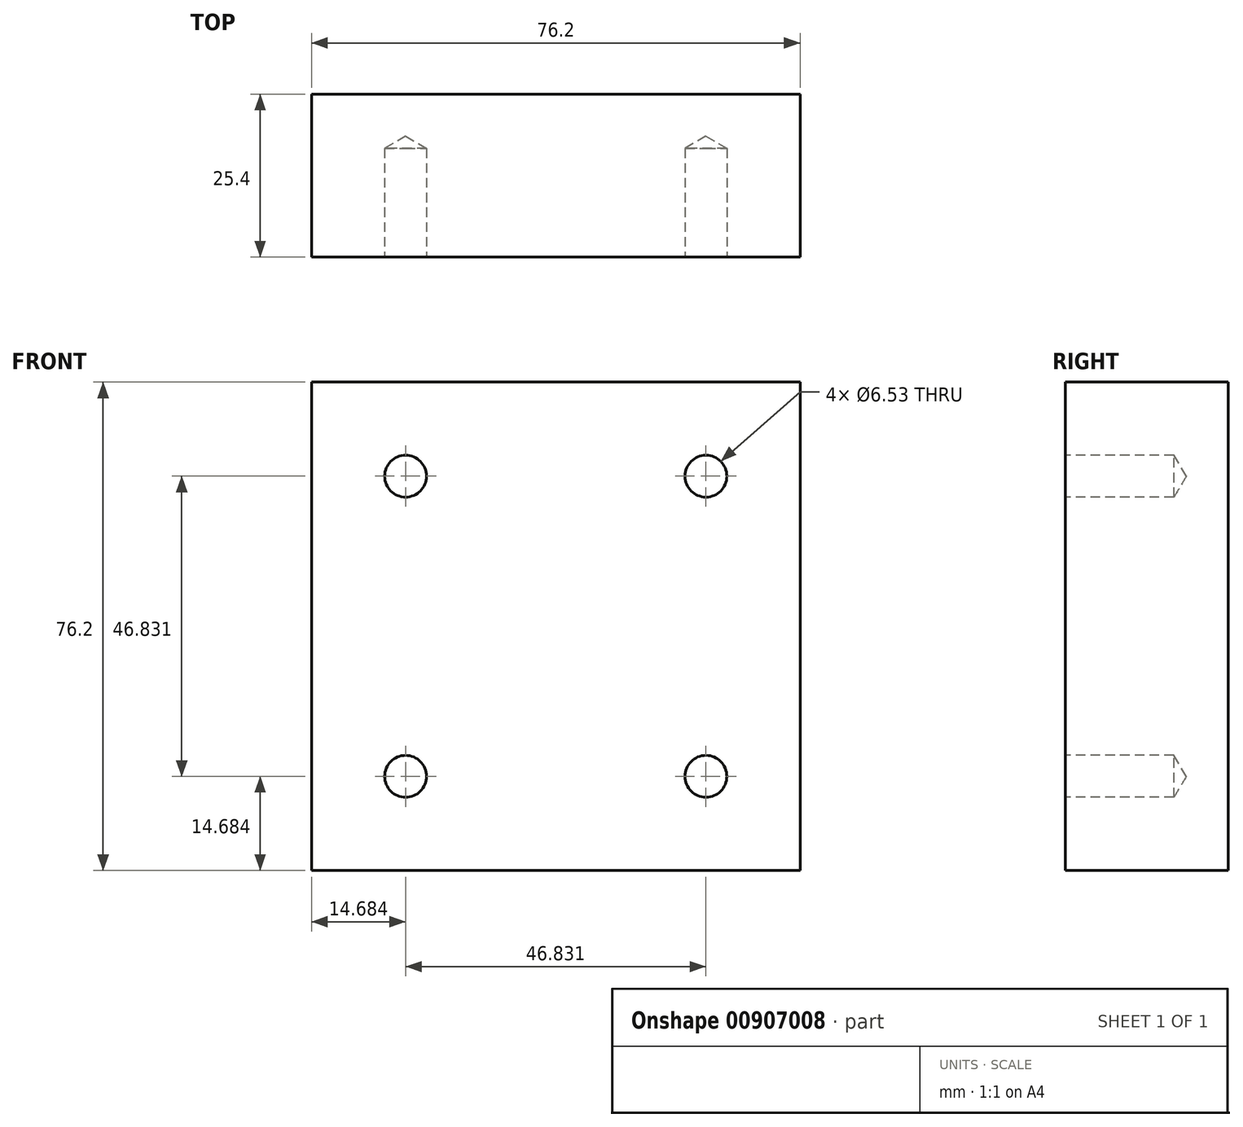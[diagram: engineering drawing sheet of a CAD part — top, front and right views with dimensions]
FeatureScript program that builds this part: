
annotation { "Feature Type Name" : "Feature", "Feature Type Description" : "" }
export const myFeature = defineFeature(function(context is Context, id is Id, definition is map)
    precondition{}
    {
        {
            var Q0;
            Q0=qCreatedBy(makeId("Front.planeOp"),FACE);
            var sketch = newSketch(context, id + "F0", { "sketchPlane" : qUnion([Q0])});
            skLineSegment(sketch, "E0.bottom", {"start": v(38.1, -38.1) * mm, "end": v(-38.1, -38.1) * mm});
            skLineSegment(sketch, "E0.top", {"start": v(38.1, 38.1) * mm, "end": v(-38.1, 38.1) * mm});
            skLineSegment(sketch, "E0.left", {"start": v(38.1, -38.1) * mm, "end": v(38.1, 38.1) * mm});
            skLineSegment(sketch, "E0.right", {"start": v(-38.1, -38.1) * mm, "end": v(-38.1, 38.1) * mm});
            skPoint(sketch, "E0.middle", {"position": v(0, 0) * mm});
            skSolve(sketch);
        }
        {
            var Q0;
            Q0=makeQuery(id+"F0.imprint","IMPRINT",FACE,{"disambiguationData":[TD([[makeQuery(id+"F0.imprint","IMPRINT",EDGE,{"derivedFrom":sQuery(id+"F0.wireOp",EDGE,"E0.bottom")}),-1.0]])]});
            extrude(context, id + "F1", {"entities" : qUnion([Q0]), "depth" : 25.4 * mm, "offsetDistance" : 25.4 * mm});
        }
        {
            var Q0;
            Q0=makeQuery(id+"F1.opExtrude","CAP_FACE",FACE,{"disambiguationData":[OSD([sQuery(id+"F0.wireOp",EDGE,"E0.bottom"),sQuery(id+"F0.wireOp",EDGE,"E0.top"),sQuery(id+"F0.wireOp",EDGE,"E0.left"),sQuery(id+"F0.wireOp",EDGE,"E0.right")])],"isStart":false});
            var sketch = newSketch(context, id + "F2", { "sketchPlane" : qUnion([Q0])});
            skLineSegment(sketch, "E1.bottom", {"start": v(23.42, 23.42) * mm, "end": v(-23.42, 23.42) * mm, "construction": true});
            skLineSegment(sketch, "E1.top", {"start": v(23.42, -23.42) * mm, "end": v(-23.42, -23.42) * mm, "construction": true});
            skLineSegment(sketch, "E1.left", {"start": v(23.42, 23.42) * mm, "end": v(23.42, -23.42) * mm, "construction": true});
            skLineSegment(sketch, "E1.right", {"start": v(-23.42, 23.42) * mm, "end": v(-23.42, -23.42) * mm, "construction": true});
            skPoint(sketch, "E1.middle", {"position": v(0, 0) * mm});
            skSolve(sketch);
        }
        {
            var Q0;
            Q0=sQuery(id+"F2.wireOp",VERTEX,"E1.bottom.end");
            var Q1;
            Q1=sQuery(id+"F2.wireOp",VERTEX,"E1.bottom.start");
            var Q2;
            Q2=sQuery(id+"F2.wireOp",VERTEX,"E1.top.start");
            var Q3;
            Q3=sQuery(id+"F2.wireOp",VERTEX,"E1.top.end");
            var Q4;
            Q4=makeQuery(id+"F1.opExtrude","SWEPT_BODY",BODY,{"disambiguationData":[OSD([sQuery(id+"F0.wireOp",EDGE,"E0.bottom"),sQuery(id+"F0.wireOp",EDGE,"E0.top"),sQuery(id+"F0.wireOp",EDGE,"E0.left"),sQuery(id+"F0.wireOp",EDGE,"E0.right")])]});
            hole(context, id + "F3", {"style" : HoleStyle.SIMPLE, "endStyle" : HoleEndStyle.BLIND, "standardTappedOrClearance" : lookupTablePath({ "standard" : "ANSI", "engagement" : "75%", "pitch" : "18 tpi", "size" : "5/16", "type" : "Tapped" }), "standardBlindInLast" : lookupTablePath({ "standard" : "ANSI", "fit" : "Free", "engagement" : "75%", "pitch" : "18 tpi", "size" : "5/16", "type" : "Clearance & tapped" }), "holeDiameter" : 6.53 * mm, "majorDiameter" : 7.94 * mm, "showTappedDepth" : true, "holeDepth" : 16.93 * mm, "isTappedThrough" : true, "tappedDepth" : 12.7 * mm, "tapClearance" : 3, "locations" : qUnion([Q0, Q1, Q2, Q3]), "scope" : qUnion([Q4])});
        }
    });
